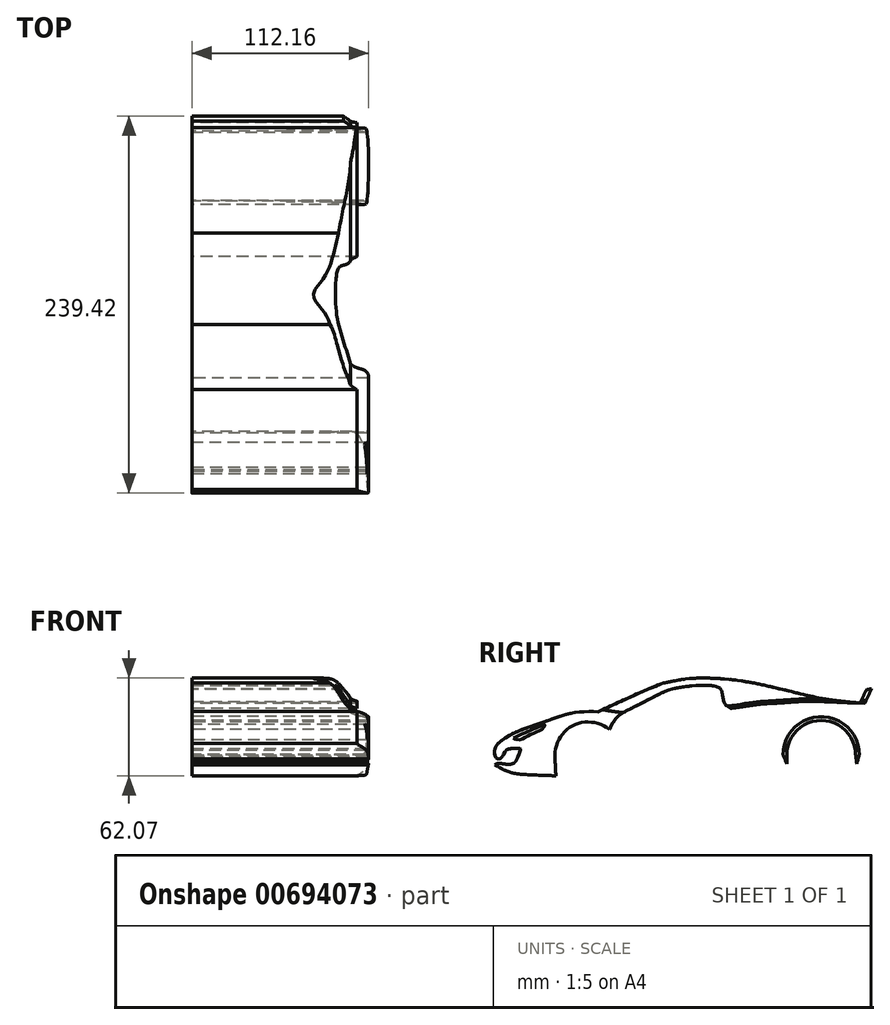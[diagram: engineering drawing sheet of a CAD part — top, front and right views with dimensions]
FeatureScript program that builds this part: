
annotation { "Feature Type Name" : "Feature", "Feature Type Description" : "" }
export const myFeature = defineFeature(function(context is Context, id is Id, definition is map)
    precondition{}
    {
        {
            var Q0;
            Q0=qCreatedBy(makeId("Front.planeOp"),FACE);
            var sketch = newSketch(context, id + "F0", { "sketchPlane" : qUnion([Q0])});
            skLineSegment(sketch, "E0", {"start": v(-52.64, 54.61) * mm, "end": v(52.63, 54.61) * mm});
            skLineSegment(sketch, "E1.bottom", {"start": v(-63.24, 52.61) * mm, "end": v(63.24, 52.61) * mm});
            skLineSegment(sketch, "E1.top", {"start": v(-63.24, -49.92) * mm, "end": v(63.24, -49.92) * mm});
            skLineSegment(sketch, "E1.left", {"start": v(-63.24, 52.61) * mm, "end": v(-63.24, -49.92) * mm});
            skLineSegment(sketch, "E1.right", {"start": v(63.24, 52.61) * mm, "end": v(63.24, -49.92) * mm});
            skFitSpline(sketch, "E2", {"points": [v(40.71, 17.64) * mm, v(36.26, 24.74) * mm, v(30.59, 33.02) * mm, v(26.7, 35.75) * mm, v(17.15, 37.11) * mm, v(3.52, 37.7) * mm, v(0, 37.68) * mm], "startDerivative": vector(-18.03, 42.44) * mm, "endDerivative": vector(-25.88, -0.48) * mm});
            skFitSpline(sketch, "E3", {"points": [v(0, -17.01) * mm, v(7.77, -17.01) * mm, v(14.58, -17.24) * mm, v(19.4, -18.82) * mm, v(24.47, -19.96) * mm, v(31.5, -17.18) * mm, v(37.24, -12.92) * mm, v(40.68, -9) * mm, v(42.15, -6.54) * mm, v(41.99, -4.74) * mm, v(37.08, -4.24) * mm, v(23.65, -5.23) * mm, v(19.23, -8.66) * mm, v(17.26, -10.63) * mm, v(14.97, -11.61) * mm, v(7.55, -11.94) * mm, v(0, -11.8) * mm], "startDerivative": vector(102.75, -3.68) * mm, "endDerivative": vector(-99.72, 2.33) * mm});
            skFitSpline(sketch, "E4", {"points": [v(28.55, -20.75) * mm, v(35.43, -21.1) * mm, v(43.28, -20.75) * mm, v(48.51, -18.2) * mm, v(50.58, -13.39) * mm, v(51.4, -3.27) * mm, v(52.16, 7.33) * mm, v(51.33, 12.7) * mm, v(49.06, 14.7) * mm, v(43.56, 16.35) * mm, v(40.71, 17.64) * mm], "startDerivative": vector(63.75, -3.6) * mm, "endDerivative": vector(-35.75, 18.5) * mm});
            skLineSegment(sketch, "E5", {"start": v(0, -17.01) * mm, "end": v(0, -49.92) * mm});
            skLineSegment(sketch, "E6", {"start": v(0, 37.68) * mm, "end": v(0, 52.61) * mm});
            skFitSpline(sketch, "E7.MirrorCS", {"points": [v(-40.71, 17.64) * mm, v(-36.26, 24.74) * mm, v(-30.59, 33.02) * mm, v(-26.7, 35.75) * mm, v(-17.15, 37.11) * mm, v(-3.52, 37.7) * mm, v(0, 37.68) * mm], "startDerivative": vector(18.03, 42.44) * mm, "endDerivative": vector(25.88, -0.48) * mm});
            skFitSpline(sketch, "E8.MirrorCS", {"points": [v(-28.55, -20.75) * mm, v(-35.43, -21.1) * mm, v(-43.28, -20.75) * mm, v(-48.51, -18.2) * mm, v(-50.58, -13.39) * mm, v(-51.4, -3.27) * mm, v(-52.16, 7.33) * mm, v(-51.33, 12.7) * mm, v(-49.06, 14.7) * mm, v(-43.56, 16.35) * mm, v(-40.71, 17.64) * mm], "startDerivative": vector(-63.75, -3.6) * mm, "endDerivative": vector(35.75, 18.5) * mm});
            skFitSpline(sketch, "E9.MirrorCS", {"points": [v(0, -17.01) * mm, v(-7.77, -17.01) * mm, v(-14.58, -17.24) * mm, v(-19.4, -18.82) * mm, v(-24.47, -19.96) * mm, v(-31.5, -17.18) * mm, v(-37.24, -12.92) * mm, v(-40.68, -9) * mm, v(-42.15, -6.54) * mm, v(-41.99, -4.74) * mm, v(-37.08, -4.24) * mm, v(-23.65, -5.23) * mm, v(-19.23, -8.66) * mm, v(-17.26, -10.63) * mm, v(-14.97, -11.61) * mm, v(-7.55, -11.94) * mm, v(0, -11.8) * mm], "startDerivative": vector(-102.75, -3.68) * mm, "endDerivative": vector(99.72, 2.33) * mm});
            skFitSpline(sketch, "E10", {"points": [v(25.8, 2.67) * mm, v(29.98, 6.14) * mm, v(34.2, 9.33) * mm, v(40.57, 11.53) * mm, v(43.81, 11.7) * mm, v(44.68, 10.72) * mm, v(43.17, 7.88) * mm, v(38.95, 4.35) * mm, v(33.22, 2.2) * mm, v(27.78, 2.15) * mm, v(25.8, 2.67) * mm]});
            skFitSpline(sketch, "E11.MirrorC", {"points": [v(-25.8, 2.67) * mm, v(-29.98, 6.14) * mm, v(-34.2, 9.33) * mm, v(-40.57, 11.53) * mm, v(-43.81, 11.7) * mm, v(-44.68, 10.72) * mm, v(-43.17, 7.88) * mm, v(-38.95, 4.35) * mm, v(-33.22, 2.2) * mm, v(-27.78, 2.15) * mm, v(-25.8, 2.67) * mm]});
            skLineSegment(sketch, "E12", {"start": v(0, -49.92) * mm, "end": v(0, 52.61) * mm});
            skLineSegment(sketch, "E13", {"start": v(28.55, -20.75) * mm, "end": v(0, -20.75) * mm});
            skSolve(sketch);
        }
        {
            var Q0;
            Q0=qCreatedBy(makeId("Right.planeOp"),FACE);
            var sketch = newSketch(context, id + "F1", { "sketchPlane" : qUnion([Q0])});
            skLineSegment(sketch, "E14", {"start": v(0, 70) * mm, "end": v(-125.25, 70) * mm});
            skLineSegment(sketch, "E15", {"start": v(-125.25, 70) * mm, "end": v(125.25, 70) * mm});
            skFitSpline(sketch, "E16", {"points": [v(-18.28, 34.08) * mm, v(-7.07, 36.3) * mm, v(5.31, 37.33) * mm, v(25.23, 36.3) * mm, v(39.68, 34.08) * mm], "startDerivative": vector(50.67, 10.97) * mm, "endDerivative": vector(53.84, -9.63) * mm});
            skFitSpline(sketch, "E17", {"points": [v(-59.79, 15.83) * mm, v(-44.92, 22.72) * mm, v(-27.57, 30.43) * mm, v(-18.28, 34.08) * mm], "startDerivative": vector(40.56, 18.9) * mm, "endDerivative": vector(30.67, 11.9) * mm});
            skFitSpline(sketch, "E18", {"points": [v(-44.98, -22.18) * mm, v(-29.34, -22.18) * mm, v(18.14, -22.18) * mm, v(58.6, -19.74) * mm, v(60.36, -17.24) * mm], "startDerivative": vector(65.5, -0.03) * mm, "endDerivative": vector(7.84, 29.28) * mm});
            skFitSpline(sketch, "E19", {"points": [v(104.56, -17.34) * mm, v(113.52, -15.4) * mm, v(121.22, -7.75) * mm, v(123.75, -3.2) * mm, v(124.4, 4.4) * mm, v(122.03, 5.88) * mm, v(118.92, 11.7) * mm, v(117.45, 16.69) * mm, v(118.6, 19.3) * mm, v(120.72, 20.62) * mm, v(120.82, 22.08) * mm], "startDerivative": vector(74.88, 1.27) * mm, "endDerivative": vector(-5.34, 29.97) * mm});
            skFitSpline(sketch, "E20", {"points": [v(-113.4, -0.78) * mm, v(-110.1, -1.88) * mm, v(-102.8, 1.42) * mm, v(-94.74, 5.28) * mm, v(-93.64, 7.75) * mm, v(-97.9, 6.24) * mm, v(-104.51, 3.35) * mm, v(-111.95, 0) * mm, v(-113.4, -0.78) * mm]});
            skFitSpline(sketch, "E21", {"points": [v(-52.56, 4.58) * mm, v(-50.01, 9.43) * mm, v(-45.92, 13.94) * mm, v(-35.93, 19.42) * mm, v(-19.58, 27.77) * mm, v(-8.75, 31.2) * mm, v(10.08, 32.68) * mm, v(17.5, 30.98) * mm, v(19.08, 27.6) * mm, v(21.05, 20.73) * mm, v(24.65, 18.08) * mm, v(26.61, 14.83) * mm, v(25.14, 10.08) * mm, v(17.12, -2.2) * mm, v(7.62, -16.28) * mm, v(-4.17, -22.16) * mm], "startDerivative": vector(45.88, 96.06) * mm, "endDerivative": vector(-159.24, -53.68) * mm});
            skFitSpline(sketch, "E22", {"points": [v(10.08, 32.68) * mm, v(24.52, 31.57) * mm, v(48.76, 26.7) * mm, v(60.15, 24.27) * mm, v(60.83, 23.1) * mm, v(57.26, 21.59) * mm], "startDerivative": vector(53.42, -1.5) * mm, "endDerivative": vector(-38.04, -10.3) * mm});
            skFitSpline(sketch, "E23", {"points": [v(26.26, 12.38) * mm, v(32.79, 12.88) * mm, v(41.75, 13.65) * mm, v(47.2, 13.95) * mm, v(49.83, 12.78) * mm, v(48.37, 7.52) * mm, v(45.15, 2.56) * mm, v(38.24, -4.55) * mm, v(29.29, -9.9) * mm, v(17.31, -12.05) * mm, v(5.24, -13.7) * mm, v(-23.97, -17.1) * mm, v(-38.47, -18.57) * mm], "startDerivative": vector(88.59, 6.6) * mm, "endDerivative": vector(-121.7, -11.71) * mm});
            skFitSpline(sketch, "E24", {"points": [v(32.79, 12.88) * mm, v(32.79, 9.66) * mm, v(29, -0.75) * mm, v(17.31, -12.05) * mm], "startDerivative": vector(1.28, -13.97) * mm, "endDerivative": vector(-30.28, -23.58) * mm});
            skFitSpline(sketch, "E25", {"points": [v(106.68, 32.68) * mm, v(109.6, 30.4) * mm, v(123.23, 32.68) * mm], "startDerivative": vector(6.5, -8.4) * mm, "endDerivative": vector(24.68, 6.8) * mm});
            skLineSegment(sketch, "E26", {"start": v(106.68, 32.68) * mm, "end": v(123.23, 32.68) * mm});
            skLineSegment(sketch, "E27", {"start": v(106.68, 21.5) * mm, "end": v(112.07, 32.68) * mm});
            skLineSegment(sketch, "E28", {"start": v(109.75, 21.38) * mm, "end": v(114.95, 32.68) * mm});
            skArc(sketch, "E29", {"start": v(-52.56, 4.58) * mm, "mid": v(-46.9, -2.73) * mm, "end": v(-44.87, -11.75) * mm});
            skArc(sketch, "E30", {"start": v(-52.56, 4.58) * mm, "mid": v(-75.06, 7.4) * mm, "end": v(-87.2, -11.75) * mm});
            skArc(sketch, "E31", {"start": v(-86.32, -11.75) * mm, "mid": v(-66.04, 8.53) * mm, "end": v(-45.76, -11.75) * mm});
            skLineSegment(sketch, "E32", {"start": v(-45.76, -11.75) * mm, "end": v(-44.98, -22.18) * mm});
            skLineSegment(sketch, "E33", {"start": v(-44.87, -11.75) * mm, "end": v(-44.98, -22.18) * mm});
            skLineSegment(sketch, "E34", {"start": v(-87.2, -11.75) * mm, "end": v(-86.5, -24.73) * mm});
            skLineSegment(sketch, "E35", {"start": v(-86.32, -11.75) * mm, "end": v(-86.5, -24.73) * mm});
            skArc(sketch, "E36", {"start": v(60.11, -11.15) * mm, "mid": v(80.67, 10.4) * mm, "end": v(103.63, -8.58) * mm});
            skLineSegment(sketch, "E37", {"start": v(104.56, -17.34) * mm, "end": v(103.63, -8.58) * mm});
            skLineSegment(sketch, "E38", {"start": v(60.36, -17.24) * mm, "end": v(60.11, -11.15) * mm});
            skArc(sketch, "E39", {"start": v(57.73, -11.41) * mm, "mid": v(81.96, 12.82) * mm, "end": v(106.19, -11.41) * mm});
            skLineSegment(sketch, "E40", {"start": v(57.73, -11.41) * mm, "end": v(60.36, -17.24) * mm});
            skLineSegment(sketch, "E41", {"start": v(104.56, -17.34) * mm, "end": v(106.19, -11.41) * mm});
            skFitSpline(sketch, "E42", {"points": [v(117.45, 16.69) * mm, v(114.86, 17.22) * mm, v(112.4, 17.48) * mm, v(109.66, 17.22) * mm, v(109.89, 15.6) * mm, v(113.19, 11.27) * mm, v(118.56, 7.97) * mm, v(122.03, 5.88) * mm], "startDerivative": vector(-21.3, 4.8) * mm, "endDerivative": vector(20.7, -13.2) * mm});
            skFitSpline(sketch, "E43", {"points": [v(121.02, 7.04) * mm, v(123.1, 7.05) * mm], "startDerivative": vector(2.06, 0) * mm, "endDerivative": vector(2.06, 0) * mm});
            skFitSpline(sketch, "E44", {"points": [v(118.77, 12.08) * mm, v(120.4, 12.1) * mm, v(121.3, 11.88) * mm], "startDerivative": vector(3.09, 0.18) * mm, "endDerivative": vector(1.94, -0.63) * mm});
            skFitSpline(sketch, "E45", {"points": [v(121.3, 11.88) * mm, v(121.77, 10.69) * mm, v(122.3, 9.39) * mm, v(123.1, 7.05) * mm], "startDerivative": vector(1.57, -4.13) * mm, "endDerivative": vector(2.02, -6.22) * mm});
            skFitSpline(sketch, "E46", {"points": [v(117.76, 18.23) * mm, v(118.49, 15.95) * mm, v(121.3, 14.9) * mm, v(122.03, 14.23) * mm], "startDerivative": vector(0.42, -7.26) * mm, "endDerivative": vector(2.1, -3.1) * mm});
            skFitSpline(sketch, "E47", {"points": [v(118.77, 12.08) * mm, v(119.41, 12.96) * mm, v(121.3, 13.22) * mm, v(122.03, 14.23) * mm], "startDerivative": vector(1.41, 3.67) * mm, "endDerivative": vector(1.5, 3.99) * mm});
            skFitSpline(sketch, "E48", {"points": [v(121.22, -7.75) * mm, v(122.65, -7.87) * mm, v(123.32, -8.54) * mm, v(122.47, -10.95) * mm, v(120.17, -14.4) * mm, v(116.99, -16.8) * mm, v(112.95, -18.91) * mm, v(110.73, -18.58) * mm, v(108.87, -17.99) * mm, v(104.56, -17.34) * mm], "startDerivative": vector(19.05, 0.3) * mm, "endDerivative": vector(-34.37, 4.18) * mm});
            skFitSpline(sketch, "E49", {"points": [v(-86.5, -24.73) * mm, v(-104.3, -24.08) * mm, v(-115.33, -22.56) * mm, v(-125.21, -17.85) * mm], "startDerivative": vector(-48.51, 1.5) * mm, "endDerivative": vector(-32.12, 18.06) * mm});
            skFitSpline(sketch, "E50", {"points": [v(-128.56, -8.72) * mm, v(-123.16, -4.24) * mm, v(-114.8, 1.62) * mm, v(-93.9, 9.52) * mm, v(-77.4, 14.84) * mm, v(-59.79, 15.83) * mm, v(-45.92, 13.94) * mm, v(-11.56, 15.15) * mm, v(24.65, 18.08) * mm, v(42.03, 20.54) * mm, v(57.26, 21.59) * mm, v(75.1, 22.52) * mm, v(109.75, 21.38) * mm, v(120.82, 22.08) * mm], "startDerivative": vector(112.35, 92.8) * mm, "endDerivative": vector(152.27, 17.85) * mm});
            skFitSpline(sketch, "E51", {"points": [v(39.68, 34.08) * mm, v(54.05, 30.88) * mm, v(83.16, 24.27) * mm, v(106.68, 21.5) * mm], "startDerivative": vector(47.62, -10.09) * mm, "endDerivative": vector(64.99, -5.37) * mm});
            skFitSpline(sketch, "E52", {"points": [v(-123.16, -4.24) * mm, v(-124.91, -6.72) * mm, v(-125.03, -12.46) * mm, v(-122.52, -14.13) * mm, v(-119.93, -11.43) * mm, v(-117.54, -8.16) * mm, v(-112.06, -7.36) * mm, v(-109.37, -7.4) * mm, v(-109.1, -8.35) * mm, v(-110.73, -12.8) * mm, v(-112.9, -16.46) * mm, v(-116.45, -17.45) * mm, v(-120.76, -17.04) * mm, v(-123.96, -17.07) * mm, v(-125.21, -17.85) * mm], "startDerivative": vector(-29.21, -29.63) * mm, "endDerivative": vector(-23.02, -19.71) * mm});
            skFitSpline(sketch, "E53", {"points": [v(-115.33, -22.56) * mm, v(-114.43, -18.92) * mm, v(-112.9, -16.46) * mm, v(-111.7, -14.93) * mm, v(-110.73, -12.8) * mm], "startDerivative": vector(2.23, 12.91) * mm, "endDerivative": vector(3.8, 9.8) * mm});
            skSolve(sketch);
        }
        {
            var Q0;
            Q0=makeQuery(id+"F1.imprint","IMPRINT",FACE,{"disambiguationData":[TD([[makeQuery(id+"F1.imprint","IMPRINT",EDGE,{"derivedFrom":sQuery(id+"F1.wireOp",EDGE,"E20")}),-1.0]])]});
            var Q1;
            {var subQ0=sQuery(id+"F1.wireOp",EDGE,"E52");var subQ1=sQuery(id+"F1.wireOp",EDGE,"E49");var subQ2=makeQuery(id+"F1.imprint","INTERSECT",VERTEX,{"derivedFrom":[subQ1,subQ0]});Q1=makeQuery(id+"F1.imprint","IMPRINT",FACE,{"disambiguationData":[TD([[makeQuery(id+"F1.imprint","IMPRINT",EDGE,{"disambiguationData":[TD([[subQ2,1.0]])],"derivedFrom":subQ1}),-1.0]])]});}
            extrude(context, id + "F2", {"entities" : qUnion([Q0, Q1]), "endBound" : BoundingType.SYMMETRIC, "depth" : 120 * mm, "offsetDistance" : 25 * mm});
        }
        {
            var Q0;
            {var subQ5=sQuery(id+"F1.wireOp",EDGE,"E16");Q0=makeQuery(id+"F1.imprint","IMPRINT",FACE,{"disambiguationData":[TD([[makeQuery(id+"F1.imprint","IMPRINT",EDGE,{"derivedFrom":subQ5}),-1.0]])]});}
            var Q1;
            Q1=makeQuery(id+"F1.imprint","IMPRINT",FACE,{"disambiguationData":[TD([[makeQuery(id+"F1.imprint","IMPRINT",EDGE,{"derivedFrom":sQuery(id+"F1.wireOp",EDGE,"E39")}),1.0]])]});
            var Q2;
            {var subQ0=sQuery(id+"F1.wireOp",EDGE,"E22");Q2=makeQuery(id+"F1.imprint","IMPRINT",FACE,{"disambiguationData":[TD([[makeQuery(id+"F1.imprint","IMPRINT",EDGE,{"derivedFrom":subQ0}),-1.0]])]});}
            extrude(context, id + "F3", {"entities" : qUnion([Q0, Q1, Q2]), "operationType" : NewBodyOperationType.ADD, "endBound" : BoundingType.SYMMETRIC, "depth" : 120 * mm, "offsetDistance" : 25 * mm});
        }
        {
            var Q0;
            {var subQ0=sQuery(id+"F0.wireOp",EDGE,"E1.right");Q0=makeQuery(id+"F0.imprint","IMPRINT",FACE,{"disambiguationData":[TD([[makeQuery(id+"F0.imprint","IMPRINT",EDGE,{"derivedFrom":subQ0}),-1.0]])]});}
            var Q1;
            Q1=sQuery(id+"F1.wireOp",EDGE,"E50");
            sweep(context, id + "F4", {"operationType" : NewBodyOperationType.REMOVE, "profiles" : qUnion([Q0]), "path" : qUnion([Q1]), "keepProfileOrientation" : true});
        }
    });
